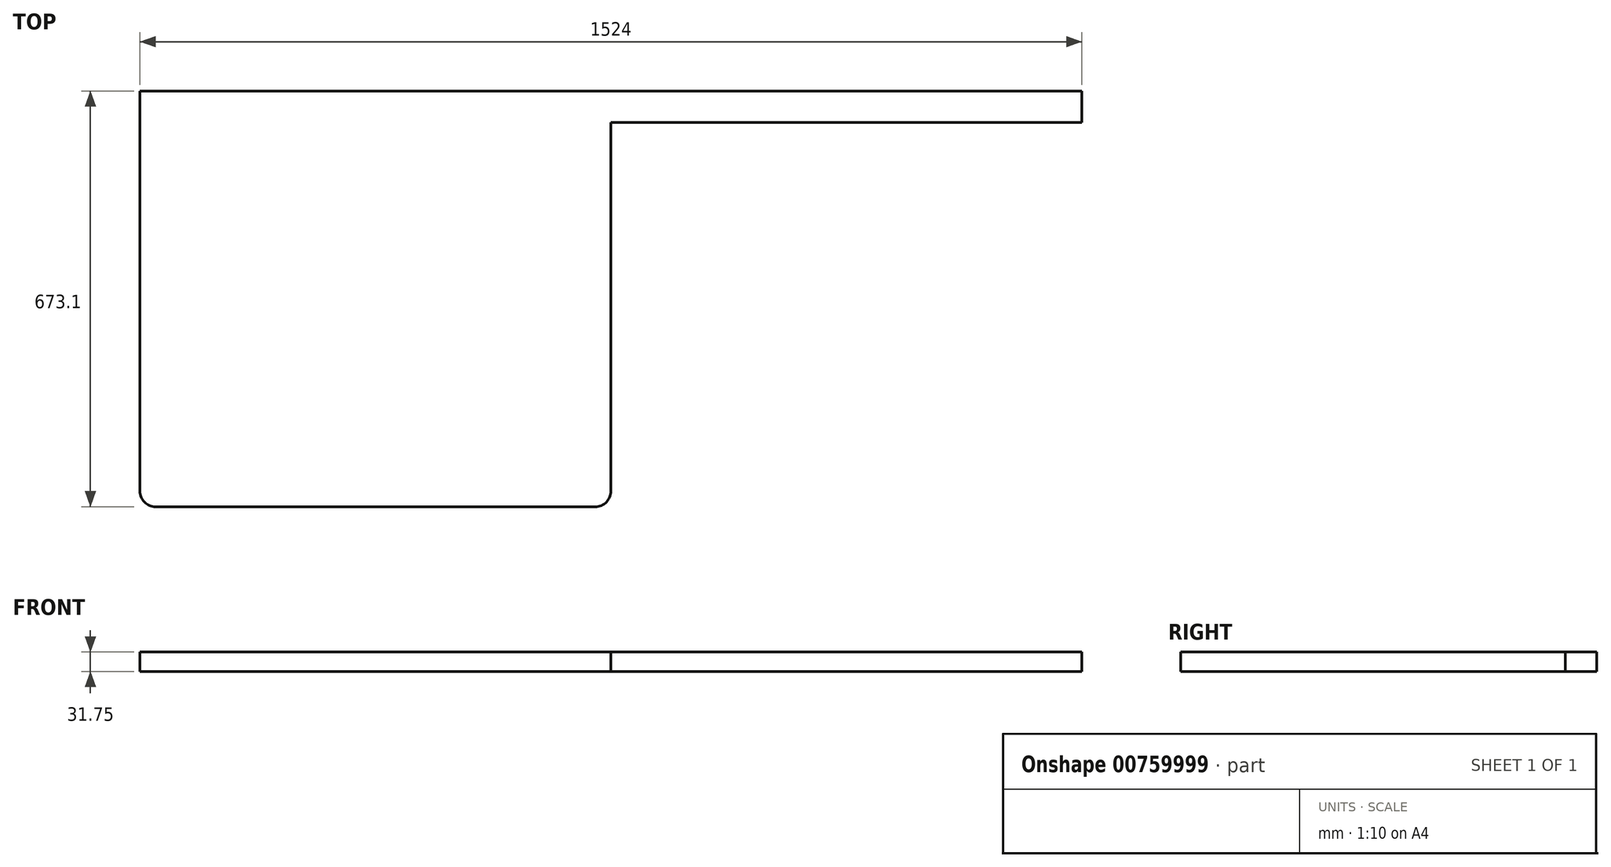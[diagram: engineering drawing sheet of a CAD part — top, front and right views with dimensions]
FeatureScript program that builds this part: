
annotation { "Feature Type Name" : "Feature", "Feature Type Description" : "" }
export const myFeature = defineFeature(function(context is Context, id is Id, definition is map)
    precondition{}
    {
        {
            var Q0;
            Q0=qCreatedBy(makeId("Top.planeOp"),FACE);
            var sketch = newSketch(context, id + "F0", { "sketchPlane" : qUnion([Q0])});
            skLineSegment(sketch, "E0.bottom", {"start": v(-25.4, 0) * mm, "end": v(-736.6, 0) * mm});
            skLineSegment(sketch, "E0.left", {"start": v(0, 25.4) * mm, "end": v(0, 622.3) * mm});
            skLineSegment(sketch, "E0.right", {"start": v(-762, 25.4) * mm, "end": v(-762, 673.1) * mm});
            skPoint(sketch, "E1.visualSharp", {"position": v(0, 0) * mm});
            skArc(sketch, "E1.filletArc", {"start": v(-25.4, 0) * mm, "mid": v(-7.44, 7.44) * mm, "end": v(0, 25.4) * mm});
            skPoint(sketch, "E2.visualSharp", {"position": v(-762, 0) * mm});
            skArc(sketch, "E2.filletArc", {"start": v(-762, 25.4) * mm, "mid": v(-754.56, 7.44) * mm, "end": v(-736.6, 0) * mm});
            skLineSegment(sketch, "E3.top", {"start": v(0, 622.3) * mm, "end": v(762, 622.3) * mm});
            skLineSegment(sketch, "E3.right", {"start": v(762, 673.1) * mm, "end": v(762, 622.3) * mm});
            skLineSegment(sketch, "E4", {"start": v(762, 673.1) * mm, "end": v(-762, 673.1) * mm});
            skSolve(sketch);
        }
        {
            var Q0;
            Q0=makeQuery(id+"F0.imprint","IMPRINT",FACE,{"disambiguationData":[TD([[makeQuery(id+"F0.imprint","IMPRINT",EDGE,{"derivedFrom":sQuery(id+"F0.wireOp",EDGE,"E0.bottom")}),-1.0]])]});
            extrude(context, id + "F1", {"entities" : qUnion([Q0]), "depth" : 31.75 * mm, "offsetDistance" : 25.4 * mm});
        }
    });
